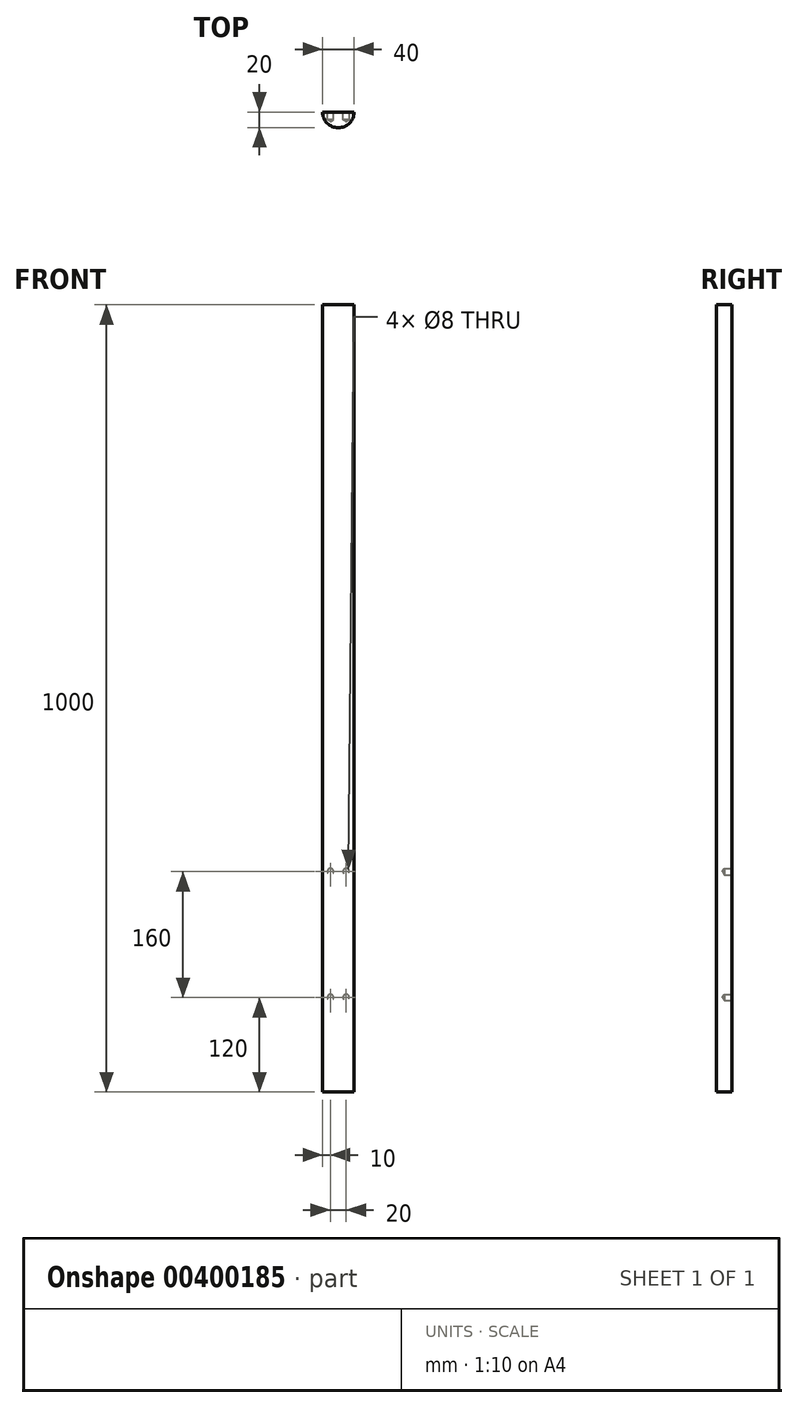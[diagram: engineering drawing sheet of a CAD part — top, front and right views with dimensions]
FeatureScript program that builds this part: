
annotation { "Feature Type Name" : "Feature", "Feature Type Description" : "" }
export const myFeature = defineFeature(function(context is Context, id is Id, definition is map)
    precondition{}
    {
        {
            var Q0;
            Q0=qCreatedBy(makeId("Top.planeOp"),FACE);
            var sketch = newSketch(context, id + "F0", { "sketchPlane" : qUnion([Q0])});
            skArc(sketch, "E0", {"start": v(-20, 0) * mm, "mid": v(0, -20) * mm, "end": v(20, 0) * mm});
            skLineSegment(sketch, "E1", {"start": v(-20, 0) * mm, "end": v(20, 0) * mm});
            skSolve(sketch);
        }
        {
            var Q0;
            Q0=makeQuery(id+"F0.imprint","IMPRINT",FACE,{"disambiguationData":[TD([[makeQuery(id+"F0.imprint","IMPRINT",EDGE,{"derivedFrom":sQuery(id+"F0.wireOp",EDGE,"E0")}),1.0]])]});
            extrude(context, id + "F1", {"entities" : qUnion([Q0]), "depth" : 1000 * mm});
        }
        {
            var Q0;
            Q0=makeQuery(id+"F1.opExtrude","SWEPT_FACE",FACE,{"disambiguationData":[OSD([sQuery(id+"F0.wireOp",EDGE,"E1")])]});
            var sketch = newSketch(context, id + "F2", { "sketchPlane" : qUnion([Q0])});
            skPoint(sketch, "E2", {"position": v(-10, 120) * mm});
            skPoint(sketch, "E3", {"position": v(10, 120) * mm});
            skPoint(sketch, "E4", {"position": v(-10, 280) * mm});
            skPoint(sketch, "E5", {"position": v(10, 280) * mm});
            skSolve(sketch);
        }
        {
            var Q0;
            Q0=sQuery(id+"F2.wireOp",VERTEX,"E4");
            var Q1;
            Q1=sQuery(id+"F2.wireOp",VERTEX,"E5");
            var Q2;
            Q2=sQuery(id+"F2.wireOp",VERTEX,"E2");
            var Q3;
            Q3=sQuery(id+"F2.wireOp",VERTEX,"E3");
            var Q4;
            Q4=makeQuery(id+"F1.opExtrude","SWEPT_BODY",BODY,{"disambiguationData":[OSD([sQuery(id+"F0.wireOp",EDGE,"E0"),sQuery(id+"F0.wireOp",EDGE,"E1")])]});
            hole(context, id + "F3", {"style" : HoleStyle.SIMPLE, "endStyle" : HoleEndStyle.BLIND, "holeDiameter" : 8 * mm, "holeDepth" : 10 * mm, "isTappedThrough" : true, "tappedDepth" : 12 * mm, "tapClearance" : 3, "startFromSketch" : true, "locations" : qUnion([Q0, Q1, Q2, Q3]), "scope" : qUnion([Q4])});
        }
    });
